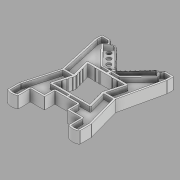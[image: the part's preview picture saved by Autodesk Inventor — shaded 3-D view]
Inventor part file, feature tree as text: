
AUTODESK INVENTOR PART (.ipt)
format: ipt  version: 2022.1 (Build 261234020, 234B)  size: 3,043,840 bytes
history: native  units: in
note: dims shown in document units (in); Inventor stores cm internally (conversion verified against a paired STEP export)
features: extrude x7, sketch x5, chamfer x4, mirror x4, plane x4, fillet x3, boolean_combine x3, other x1, projected_geometry x1
ambient origin geometry x8: Origin, YZ Plane, XZ Plane, XY Plane, X Axis, Y Axis, Z Axis, Center Point
bodies: Solid1 (feature_tree), Solid2 (feature_tree), Solid3 (feature_tree), Solid4 (feature_tree)
feature tree (32):
  sketch  "Sketch1"  dims[d7=7.9381in d16=3.1568in]
  extrude  "Extrusion1"  Depth=3.1568in
  extrude  "Extrusion2"  Depth=0.6164in
  extrude  "Extrusion3"  Depth=0.7283in
  extrude  "Extrusion4"  Depth=0.6398in
  chamfer  "Chamfer1"  Distance=0.0197in
  chamfer  "Chamfer2"  Distance=0.0266in
  chamfer  "Chamfer3"  Distance=0.7677in
  chamfer  "Chamfer4"  Distance=0.748in
  sketch  "Sketch2"  dims[d17=2.5927in d29=0.6164in]
  fillet  "Fillet1"  Radius=0.0659in
  fillet  "Fillet2"  Radius=0.0659in
  fillet  "Fillet3"  Radius=0.748in
  extrude  "Extrusion5"  Depth=0.0236in
  mirror  "Mirror1"
  boolean_combine  "Combine1"
  extrude  "Extrusion6"  Depth=0.0236in
  plane  "Work Plane1"
  mirror  "Mirror2"
  boolean_combine  "Combine2"
  plane  "Work Plane4"
  extrude  "Extrusion7"  Depth=0.0236in
  mirror  "Mirror3"
  mirror  "Mirror4"
  boolean_combine  "Combine3"
  other  "Image1"
  sketch  "Sketch3"  dims[d31=1.9685in d37=0.7283in]
  sketch  "Sketch4"  dims[d38=0.0276in d39=0.6398in]
  plane  "Work Plane2"
  plane  "Work Plane3"
  sketch  "Sketch5"  dims[d40=0.9173in d41=0.0197in d42=0.0266in d43=0.7677in d44=0.748in d45=0.0659in d46=0.0659in d47=0.748in d48=0.187in d49=2.2441in d50=2.8543in d51=0.3839in d52=0.4528in d53=0.0591in d54=0.1575in d55=0.1903in d56=0.1476in d57=1.0429in d58=0.1634in d59=0.0787in d61=2.9211in d62=0.4426in d78=0.1181in d92=0.0787in d114=0.1378in d128=0.0591in d129=0.1181in d139=0.0787in d148=0.1378in d149=1.7913in d150=0.1575in d151=0.0827in d159=0.0787in d162=0.0787in d164=0.0591in d166=0.0787in d245=0.0594in d246=0.7049in d247=0.3055in d248=0.9271in d249=0.8975in d250=0.3097in d251=0.923in d252=0.7244in d253=0.0in d254=1.851in d255=1.4294in d256=1.2977in d257=3.6187in d258=0.0737in d259=2.5252in d260=0.1721in d261=0.1181in d262=0.0984in d263=1.9073in d264=2.0451in d265=2.3942in d266=0.0364in d267=2.309in d268=4.4539in d269=4.3714in d270=1.466in d271=1.466in d272=1.8095in d273=4.2023in d274=1.2451in d275=1.4789in d276=3.157in d277=3.1585in d279=0.3051in d281=1.5748in d283=0.4724in d284=0.3937in d286=0.3937in d292=0.328in d293=1.4776in d294=1.4695in d296=0.1181in d297=0.0in d308=0.7874in d309=0.0in d310=0.4331in d311=0.0in d312=0.0787in d313=0.1575in d314=0.4331in d315=0.0in d316=0.1772in d317=0.0787in d318=45.0deg d319=0.1772in d320=0.0787in d321=45.0deg d322=0.2505in d323=0.0787in d324=45.0deg d325=0.2295in d326=0.0787in d327=45.0deg d328=0.0787in d329=0.0787in d330=0.8484in d331=0.0551in d332=3.1496in d334=0.2362in d335=0.3937in d337=0.3937in d339=0.0394in d340=0.0in d341=0.4921in d342=0.8071in d343=0.4921in d344=0.8071in d345=0.063in d346=0.7874in d347=0.063in d348=0.7874in d349=0.063in d350=0.7874in d351=0.063in d352=0.7874in d353=0.0236in d354=0.0in d355=0.1378in d356=0.2953in d357=0.2953in d358=0.0591in d359=0.7874in d360=0.0591in d361=0.7874in d362=0.0591in d363=0.7874in d364=0.0236in d365=0.0in]
  projected_geometry  "Projected Loop1"
